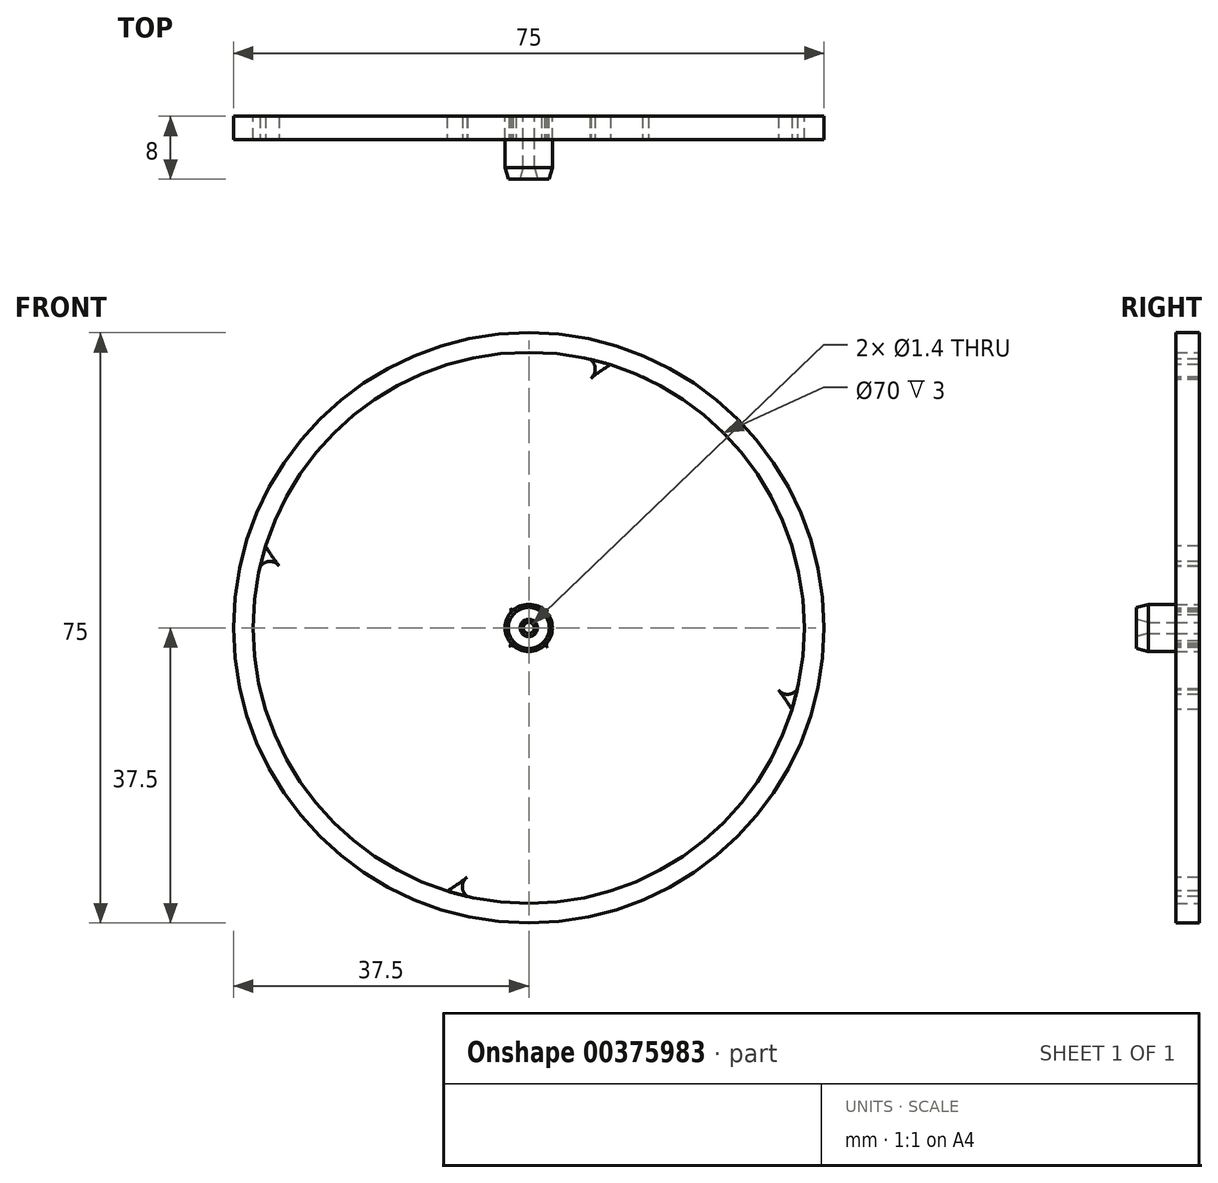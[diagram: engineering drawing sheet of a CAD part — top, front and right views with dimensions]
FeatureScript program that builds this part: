
annotation { "Feature Type Name" : "Feature", "Feature Type Description" : "" }
export const myFeature = defineFeature(function(context is Context, id is Id, definition is map)
    precondition{}
    {
        {
            var Q0;
            Q0=qCreatedBy(makeId("Front.planeOp"),FACE);
            var sketch = newSketch(context, id + "F0", { "sketchPlane" : qUnion([Q0])});
            skCircle(sketch, "E0", {"center": v(0, 0) * mm, "radius": 37.5 * mm});
            skCircle(sketch, "E1", {"center": v(0, 0) * mm, "radius": 0.7 * mm});
            skCircle(sketch, "E2", {"center": v(0, 0) * mm, "radius": 3 * mm});
            skCircle(sketch, "E3", {"center": v(0, 0) * mm, "radius": 35 * mm});
            skSolve(sketch);
        }
        {
            var Q0;
            Q0=qSketchRegion(id+"F0",true);
            var Q1;
            Q1=makeQuery(id+"F0.imprint","IMPRINT",FACE,{"disambiguationData":[TD([[makeQuery(id+"F0.imprint","IMPRINT",EDGE,{"derivedFrom":sQuery(id+"F0.wireOp",EDGE,"E1")}),-1.0]])]});
            extrude(context, id + "F1", {"entities" : qUnion([Q0, Q1]), "depth" : 3 * mm});
        }
        {
            var Q0;
            Q0=makeQuery(id+"F1.opExtrude","CAP_FACE",FACE,{"disambiguationData":[OSD([sQuery(id+"F0.wireOp",EDGE,"E0"),sQuery(id+"F0.wireOp",EDGE,"E3")])],"isStart":false});
            var sketch = newSketch(context, id + "F2", { "sketchPlane" : qUnion([Q0])});
            skLineSegment(sketch, "E4", {"start": v(1, 34.99) * mm, "end": v(2.77, 1.14) * mm});
            skLineSegment(sketch, "E5", {"start": v(-1, 34.99) * mm, "end": v(-2.77, 1.14) * mm});
            skLineSegment(sketch, "E6.1.0", {"start": v(-29.8, -18.36) * mm, "end": v(0.4, -2.97) * mm});
            skLineSegment(sketch, "E6.1.1", {"start": v(-30.8, -16.63) * mm, "end": v(-2.38, 1.83) * mm});
            skLineSegment(sketch, "E6.2.0", {"start": v(30.8, -16.63) * mm, "end": v(2.38, 1.83) * mm});
            skLineSegment(sketch, "E6.2.1", {"start": v(29.8, -18.36) * mm, "end": v(-0.4, -2.97) * mm});
            skPoint(sketch, "E6.center", {"position": v(0, 0) * mm});
            skArc(sketch, "E7", {"start": v(-30.8, -16.63) * mm, "mid": v(-30.31, -17.5) * mm, "end": v(-29.8, -18.36) * mm});
            skCircle(sketch, "E8", {"center": v(0, 0) * mm, "radius": 3 * mm});
            skArc(sketch, "E9.trimOffspring", {"start": v(1, 34.99) * mm, "mid": v(0, 35) * mm, "end": v(-1, 34.99) * mm});
            skArc(sketch, "E10.trimOffspring", {"start": v(29.8, -18.36) * mm, "mid": v(30.31, -17.5) * mm, "end": v(30.8, -16.63) * mm});
            skCircle(sketch, "E11", {"center": v(0, 0) * mm, "radius": 0.7 * mm});
            skSolve(sketch);
        }
        {
            var Q0;
            {var subQ2=sQuery(id+"F2.wireOp",EDGE,"E7");Q0=makeQuery(id+"F2.imprint","IMPRINT",FACE,{"disambiguationData":[TD([[makeQuery(id+"F2.imprint","IMPRINT",EDGE,{"derivedFrom":subQ2}),-1.0]])]});}
            var sketch = newSketch(context, id + "F3", { "sketchPlane" : qUnion([Q0])});
            skFitSpline(sketch, "E12", {"points": [v(-2.13, 2) * mm, v(-2.65, 4.3) * mm, v(-2.74, 9.9) * mm, v(0, 21.11) * mm, v(10.38, 33.43) * mm], "startDerivative": vector(-6.91, 17.48) * mm, "endDerivative": vector(42.25, 24.9) * mm});
            skFitSpline(sketch, "E13.0", {"points": [v(-0.27, 2.74) * mm, v(-0.33, 2.88) * mm, v(-0.41, 3.13) * mm, v(-0.5, 3.47) * mm, v(-0.57, 3.84) * mm, v(-0.64, 4.3) * mm, v(-0.7, 4.89) * mm, v(-0.75, 5.54) * mm, v(-0.79, 6.26) * mm, v(-0.82, 7.3) * mm, v(-0.81, 8.76) * mm, v(-0.69, 10.68) * mm, v(-0.4, 12.76) * mm, v(0.18, 15.7) * mm, v(1.13, 18.79) * mm, v(2.53, 21.89) * mm, v(4.24, 24.93) * mm, v(6.96, 28.48) * mm, v(9.8, 30.76) * mm, v(11.4, 31.7) * mm]});
            skPoint(sketch, "E14.visualSharp", {"position": v(10.36, 33.42) * mm});
            skArc(sketch, "E14.filletArc", {"start": v(7.87, 31.7) * mm, "mid": v(8.44, 32.94) * mm, "end": v(7.78, 34.12) * mm});
            skPoint(sketch, "E15.visualSharp", {"position": v(11.37, 31.7) * mm});
            skArc(sketch, "E15.filletArc", {"start": v(15.2, 31.53) * mm, "mid": v(13.12, 32.1) * mm, "end": v(11.05, 31.5) * mm});
            skArc(sketch, "E16.filletArc", {"start": v(-2.43, 1.63) * mm, "mid": v(-2.27, 2.05) * mm, "end": v(-2.3, 2.5) * mm});
            skPoint(sketch, "E17.visualSharp", {"position": v(-0.33, 2.9) * mm});
            skArc(sketch, "E17.filletArc", {"start": v(-0.46, 3.3) * mm, "mid": v(-0.28, 3.03) * mm, "end": v(0.02, 2.92) * mm});
            skArc(sketch, "E18", {"start": v(0.02, 2.92) * mm, "mid": v(-1.37, 2.59) * mm, "end": v(-2.43, 1.63) * mm});
            skArc(sketch, "E19", {"start": v(15.2, 31.53) * mm, "mid": v(11.57, 33.03) * mm, "end": v(7.78, 34.12) * mm});
            skSolve(sketch);
        }
        {
            var Q0;
            Q0=qSketchRegion(id+"F3",true);
            extrude(context, id + "F4", {"entities" : qUnion([Q0]), "oppositeDirection" : true, "depth" : 3 * mm});
        }
        {
            var Q0;
            Q0=makeQuery(id+"F4.opExtrude","SWEPT_BODY",BODY,{"disambiguationData":[OSD([sQuery(id+"F3.wireOp",EDGE,"E12"),sQuery(id+"F3.wireOp",EDGE,"E13.0"),sQuery(id+"F3.wireOp",EDGE,"E14.filletArc"),sQuery(id+"F3.wireOp",EDGE,"E15.filletArc"),sQuery(id+"F3.wireOp",EDGE,"E16.filletArc"),sQuery(id+"F3.wireOp",EDGE,"E17.filletArc"),sQuery(id+"F3.wireOp",EDGE,"E18"),sQuery(id+"F3.wireOp",EDGE,"E19")])]});
            var Q1;
            Q1=makeQuery(id+"F1.opExtrude","CAP_EDGE",EDGE,{"disambiguationData":[OSD([sQuery(id+"F0.wireOp",EDGE,"E2")])],"isStart":false});
            circularPattern(context, id + "F5", {"entities" : qUnion([Q0]), "axis" : qUnion([Q1]), "angle" : 360 * degree, "instanceCount" : 4, "equalSpace" : true});
        }
        {
            var Q0;
            Q0=makeQuery(id+"F1.opExtrude","CAP_FACE",FACE,{"disambiguationData":[OSD([sQuery(id+"F0.wireOp",EDGE,"E1"),sQuery(id+"F0.wireOp",EDGE,"E2")])],"isStart":false});
            var sketch = newSketch(context, id + "F6", { "sketchPlane" : qUnion([Q0])});
            skSolve(sketch);
        }
        {
            var Q0;
            Q0=makeQuery(id+"F6.imprint","IMPRINT",FACE,{"disambiguationData":[TD([[makeQuery(id+"F6.imprint","IMPRINT",EDGE,{"derivedFrom":makeQuery(id+"F1.opExtrude","CAP_EDGE",EDGE,{"disambiguationData":[OSD([sQuery(id+"F0.wireOp",EDGE,"E1")])],"isStart":false})}),-1.0]])]});
            var sketch = newSketch(context, id + "F7", { "sketchPlane" : qUnion([Q0])});
            skCircle(sketch, "E20.0.0", {"center": v(0, 0) * mm, "radius": 3 * mm});
            skCircle(sketch, "E21.0", {"center": v(0, 0) * mm, "radius": 0.7 * mm});
            skSolve(sketch);
        }
        {
            var Q0;
            Q0=qSketchRegion(id+"F7",true);
            extrude(context, id + "F8", {"entities" : qUnion([Q0]), "depth" : 5 * mm});
        }
        {
            var Q0;
            Q0=makeQuery(id+"F8.opExtrude","CAP_EDGE",EDGE,{"disambiguationData":[OSD([sQuery(id+"F7.wireOp",EDGE,"E21.0")])],"isStart":false});
            var Q1;
            Q1=makeQuery(id+"F8.opExtrude","CAP_EDGE",EDGE,{"disambiguationData":[OSD([sQuery(id+"F7.wireOp",EDGE,"E20.0.0")])],"isStart":false});
            chamfer(context, id + "F9", {"entities" : qUnion([Q0, Q1]), "chamferType" : ChamferType.TWO_OFFSETS, "width1" : 1.5 * mm, "oppositeDirection" : false, "width2" : 0.4 * mm, "tangentPropagation" : true});
        }
    });
